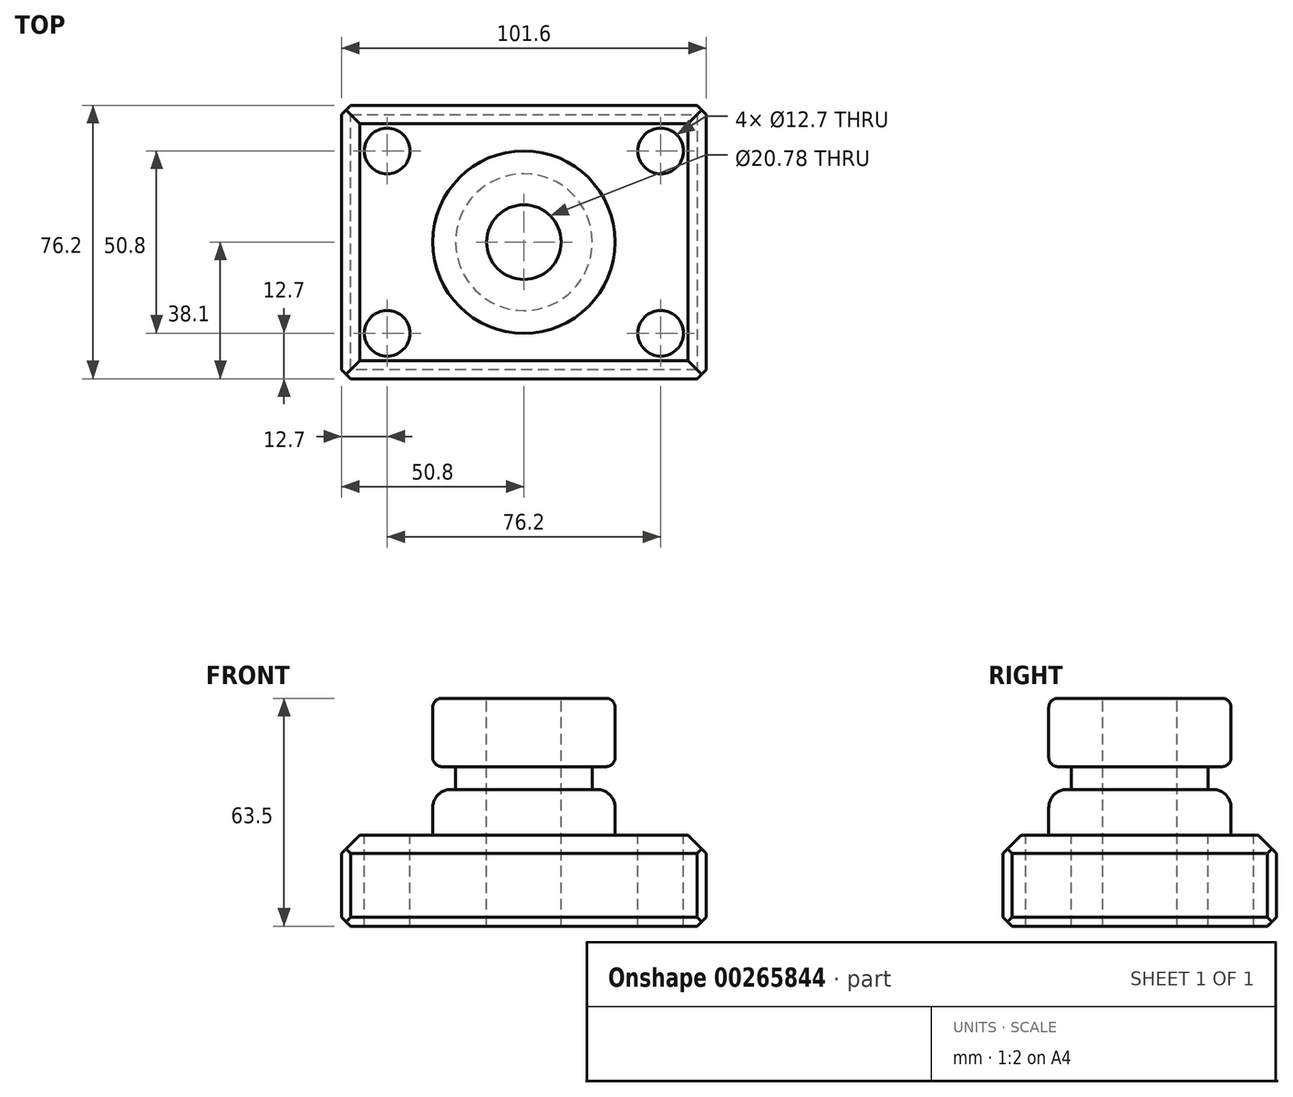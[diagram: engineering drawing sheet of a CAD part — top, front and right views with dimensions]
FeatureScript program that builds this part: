
annotation { "Feature Type Name" : "Feature", "Feature Type Description" : "" }
export const myFeature = defineFeature(function(context is Context, id is Id, definition is map)
    precondition{}
    {
        {
            var Q0;
            Q0=qCreatedBy(makeId("Top.planeOp"),FACE);
            var sketch = newSketch(context, id + "F0", { "sketchPlane" : qUnion([Q0])});
            skLineSegment(sketch, "E0.bottom", {"start": v(50.8, 38.1) * mm, "end": v(-50.8, 38.1) * mm});
            skLineSegment(sketch, "E0.top", {"start": v(50.8, -38.1) * mm, "end": v(-50.8, -38.1) * mm});
            skLineSegment(sketch, "E0.left", {"start": v(50.8, 38.1) * mm, "end": v(50.8, -38.1) * mm});
            skLineSegment(sketch, "E0.right", {"start": v(-50.8, 38.1) * mm, "end": v(-50.8, -38.1) * mm});
            skPoint(sketch, "E0.middle", {"position": v(0, 0) * mm});
            skSolve(sketch);
        }
        {
            var Q0;
            Q0=makeQuery(id+"F0.imprint","IMPRINT",FACE,{"disambiguationData":[TD([[makeQuery(id+"F0.imprint","IMPRINT",EDGE,{"derivedFrom":sQuery(id+"F0.wireOp",EDGE,"E0.bottom")}),1.0]])]});
            extrude(context, id + "F1", {"entities" : qUnion([Q0]), "depth" : 25.4 * mm});
        }
        {
            var Q0;
            Q0=makeQuery(id+"F1.opExtrude","CAP_FACE",FACE,{"disambiguationData":[OSD([sQuery(id+"F0.wireOp",EDGE,"E0.bottom"),sQuery(id+"F0.wireOp",EDGE,"E0.top"),sQuery(id+"F0.wireOp",EDGE,"E0.left"),sQuery(id+"F0.wireOp",EDGE,"E0.right")])],"isStart":false});
            var sketch = newSketch(context, id + "F2", { "sketchPlane" : qUnion([Q0])});
            skCircle(sketch, "E1", {"center": v(-38.1, 25.4) * mm, "radius": 6.35 * mm});
            skCircle(sketch, "E2", {"center": v(38.1, 25.4) * mm, "radius": 6.35 * mm});
            skCircle(sketch, "E3", {"center": v(38.1, -25.4) * mm, "radius": 6.35 * mm});
            skCircle(sketch, "E4", {"center": v(-38.1, -25.4) * mm, "radius": 6.35 * mm});
            skSolve(sketch);
        }
        {
            var Q0;
            Q0 = qSketchRegion(id + "F2", true);
            extrude(context, id + "F3", {"entities" : qUnion([Q0]), "operationType" : NewBodyOperationType.REMOVE, "oppositeDirection" : true, "depth" : 25.4 * mm});
        }
        {
            var Q0;
            Q0=qCreatedBy(makeId("Front.planeOp"),FACE);
            var sketch = newSketch(context, id + "F4", { "sketchPlane" : qUnion([Q0])});
            skLineSegment(sketch, "E5.bottom", {"start": v(0, 25.4) * mm, "end": v(-25.4, 25.4) * mm});
            skLineSegment(sketch, "E5.top", {"start": v(0, 63.5) * mm, "end": v(-25.4, 63.5) * mm});
            skLineSegment(sketch, "E5.left", {"start": v(0, 25.4) * mm, "end": v(0, 63.5) * mm});
            skLineSegment(sketch, "E5.right", {"start": v(-25.4, 25.4) * mm, "end": v(-25.4, 63.5) * mm});
            skSolve(sketch);
        }
        {
            var Q0;
            Q0 = qSketchRegion(id + "F4", true);
            var Q1;
            Q1=sQuery(id+"F4.wireOp",EDGE,"E5.left");
            revolve(context, id + "F5", {"operationType" : NewBodyOperationType.ADD, "entities" : qUnion([Q0]), "axis" : qUnion([Q1]), "revolveType" : RevolveType.FULL});
        }
        {
            var Q0;
            Q0=qCreatedBy(makeId("Right.planeOp"),FACE);
            var sketch = newSketch(context, id + "F6", { "sketchPlane" : qUnion([Q0])});
            skLineSegment(sketch, "E6.bottom", {"start": v(-49.53, 44.45) * mm, "end": v(-19.05, 44.45) * mm});
            skLineSegment(sketch, "E6.top", {"start": v(-49.53, 38.1) * mm, "end": v(-19.05, 38.1) * mm});
            skLineSegment(sketch, "E6.left", {"start": v(-49.53, 44.45) * mm, "end": v(-49.53, 38.1) * mm});
            skLineSegment(sketch, "E6.right", {"start": v(-19.05, 44.45) * mm, "end": v(-19.05, 38.1) * mm});
            skPoint(sketch, "E6.middle", {"position": v(-34.3, 41.28) * mm});
            skSolve(sketch);
        }
        {
            var Q0;
            Q0 = qSketchRegion(id + "F6", true);
            var Q1;
            Q1=makeQuery(id+"F5.opRevolve","SWEPT_FACE",FACE,{"disambiguationData":[OSD([sQuery(id+"F4.wireOp",EDGE,"E5.right")])]});
            revolve(context, id + "F7", {"operationType" : NewBodyOperationType.REMOVE, "entities" : qUnion([Q0]), "axis" : qUnion([Q1]), "revolveType" : RevolveType.FULL, "oppositeDirection" : true});
        }
        {
            var Q0;
            Q0=makeQuery(id+"F7.boolean.opBoolean","INTERSECT",EDGE,{"derivedFrom":[makeQuery(id+"F5.opRevolve","SWEPT_FACE",FACE,{"disambiguationData":[OSD([sQuery(id+"F4.wireOp",EDGE,"E5.right")])]}),makeQuery(id+"F7.opRevolve","SWEPT_FACE",FACE,{"disambiguationData":[OSD([sQuery(id+"F6.wireOp",EDGE,"E6.top")])]})]});
            fillet(context, id + "F8", {"entities" : qUnion([Q0]), "radius" : 5.08 * mm, "tangentPropagation" : true, "allowEdgeOverflow" : false});
        }
        {
            var Q0;
            Q0=makeQuery(id+"F1.opExtrude","CAP_EDGE",EDGE,{"disambiguationData":[OSD([sQuery(id+"F0.wireOp",EDGE,"E0.top")])],"isStart":false});
            var Q1;
            Q1=makeQuery(id+"F1.opExtrude","CAP_EDGE",EDGE,{"disambiguationData":[OSD([sQuery(id+"F0.wireOp",EDGE,"E0.left")])],"isStart":false});
            var Q2;
            Q2=makeQuery(id+"F1.opExtrude","CAP_EDGE",EDGE,{"disambiguationData":[OSD([sQuery(id+"F0.wireOp",EDGE,"E0.bottom")])],"isStart":false});
            var Q3;
            Q3=makeQuery(id+"F1.opExtrude","CAP_EDGE",EDGE,{"disambiguationData":[OSD([sQuery(id+"F0.wireOp",EDGE,"E0.right")])],"isStart":false});
            chamfer(context, id + "F9", {"entities" : qUnion([Q0, Q1, Q2, Q3]), "width" : 5.08 * mm, "tangentPropagation" : true});
        }
        {
            var Q0;
            Q0=makeQuery(id+"F5.opRevolve","SWEPT_EDGE",EDGE,{"disambiguationData":[OSD([sQuery(id+"F4.wireOp",EDGE,"E5.bottom"),sQuery(id+"F4.wireOp",EDGE,"E5.right")])]});
            var Q1;
            {var subQ0=makeQuery(id+"F7.opRevolve","SWEPT_FACE",FACE,{"disambiguationData":[OSD([sQuery(id+"F6.wireOp",EDGE,"E6.top")])]});var subQ1=makeQuery(id+"F5.opRevolve","SWEPT_FACE",FACE,{"disambiguationData":[OSD([sQuery(id+"F4.wireOp",EDGE,"E5.right")])]});Q1=makeQuery(id+"F8.opFillet","BLEND_EDGE",EDGE,{"blendedFrom":[makeQuery(id+"F7.boolean.opBoolean","INTERSECT",EDGE,{"derivedFrom":[subQ1,subQ0]}),makeQuery(id+"F7.boolean.opBoolean","SPLIT",FACE,{"disambiguationData":[TD([subQ0])],"derivedFrom":subQ1})],"blendedInto":[makeQuery(id+"F7.boolean.opBoolean","SPLIT",FACE,{"disambiguationData":[TD([subQ0])],"derivedFrom":subQ1})]});}
            var Q2;
            Q2=makeQuery(id+"F7.boolean.opBoolean","INTERSECT",EDGE,{"derivedFrom":[makeQuery(id+"F5.opRevolve","SWEPT_FACE",FACE,{"disambiguationData":[OSD([sQuery(id+"F4.wireOp",EDGE,"E5.right")])]}),makeQuery(id+"F7.opRevolve","SWEPT_FACE",FACE,{"disambiguationData":[OSD([sQuery(id+"F6.wireOp",EDGE,"E6.bottom")])]})]});
            var Q3;
            Q3=makeQuery(id+"F5.opRevolve","SWEPT_EDGE",EDGE,{"disambiguationData":[OSD([sQuery(id+"F4.wireOp",EDGE,"E5.top"),sQuery(id+"F4.wireOp",EDGE,"E5.right")])]});
            fillet(context, id + "F10", {"entities" : qUnion([Q0, Q1, Q2, Q3]), "radius" : 2.54 * mm, "tangentPropagation" : true, "allowEdgeOverflow" : false});
        }
        {
            var Q0;
            Q0=makeQuery(id+"F1.opExtrude","CAP_EDGE",EDGE,{"disambiguationData":[OSD([sQuery(id+"F0.wireOp",EDGE,"E0.top")])],"isStart":true});
            var Q1;
            Q1=makeQuery(id+"F1.opExtrude","CAP_EDGE",EDGE,{"disambiguationData":[OSD([sQuery(id+"F0.wireOp",EDGE,"E0.left")])],"isStart":true});
            var Q2;
            Q2=makeQuery(id+"F1.opExtrude","CAP_EDGE",EDGE,{"disambiguationData":[OSD([sQuery(id+"F0.wireOp",EDGE,"E0.bottom")])],"isStart":true});
            var Q3;
            Q3=makeQuery(id+"F1.opExtrude","CAP_EDGE",EDGE,{"disambiguationData":[OSD([sQuery(id+"F0.wireOp",EDGE,"E0.right")])],"isStart":true});
            chamfer(context, id + "F11", {"entities" : qUnion([Q0, Q1, Q2, Q3]), "width" : 2.54 * mm, "tangentPropagation" : true});
        }
        {
            var Q0;
            Q0=makeQuery(id+"F1.opExtrude","SWEPT_EDGE",EDGE,{"disambiguationData":[OSD([sQuery(id+"F0.wireOp",EDGE,"E0.bottom"),sQuery(id+"F0.wireOp",EDGE,"E0.right")])]});
            var Q1;
            Q1=makeQuery(id+"F1.opExtrude","SWEPT_EDGE",EDGE,{"disambiguationData":[OSD([sQuery(id+"F0.wireOp",EDGE,"E0.top"),sQuery(id+"F0.wireOp",EDGE,"E0.right")])]});
            var Q2;
            Q2=makeQuery(id+"F1.opExtrude","SWEPT_EDGE",EDGE,{"disambiguationData":[OSD([sQuery(id+"F0.wireOp",EDGE,"E0.bottom"),sQuery(id+"F0.wireOp",EDGE,"E0.left")])]});
            var Q3;
            Q3=makeQuery(id+"F1.opExtrude","SWEPT_EDGE",EDGE,{"disambiguationData":[OSD([sQuery(id+"F0.wireOp",EDGE,"E0.top"),sQuery(id+"F0.wireOp",EDGE,"E0.left")])]});
            chamfer(context, id + "F12", {"entities" : qUnion([Q0, Q1, Q2, Q3]), "width" : 2.54 * mm, "tangentPropagation" : true});
        }
        {
            var Q0;
            Q0=makeQuery(id+"F5.opRevolve","SWEPT_FACE",FACE,{"disambiguationData":[OSD([sQuery(id+"F4.wireOp",EDGE,"E5.top")])]});
            var sketch = newSketch(context, id + "F13", { "sketchPlane" : qUnion([Q0])});
            skCircle(sketch, "E7", {"center": v(0, 0) * mm, "radius": 10.39 * mm});
            skSolve(sketch);
        }
        {
            var Q0;
            Q0 = qSketchRegion(id + "F13", true);
            extrude(context, id + "F14", {"entities" : qUnion([Q0]), "operationType" : NewBodyOperationType.REMOVE, "oppositeDirection" : true, "depth" : 76.2 * mm});
        }
    });
